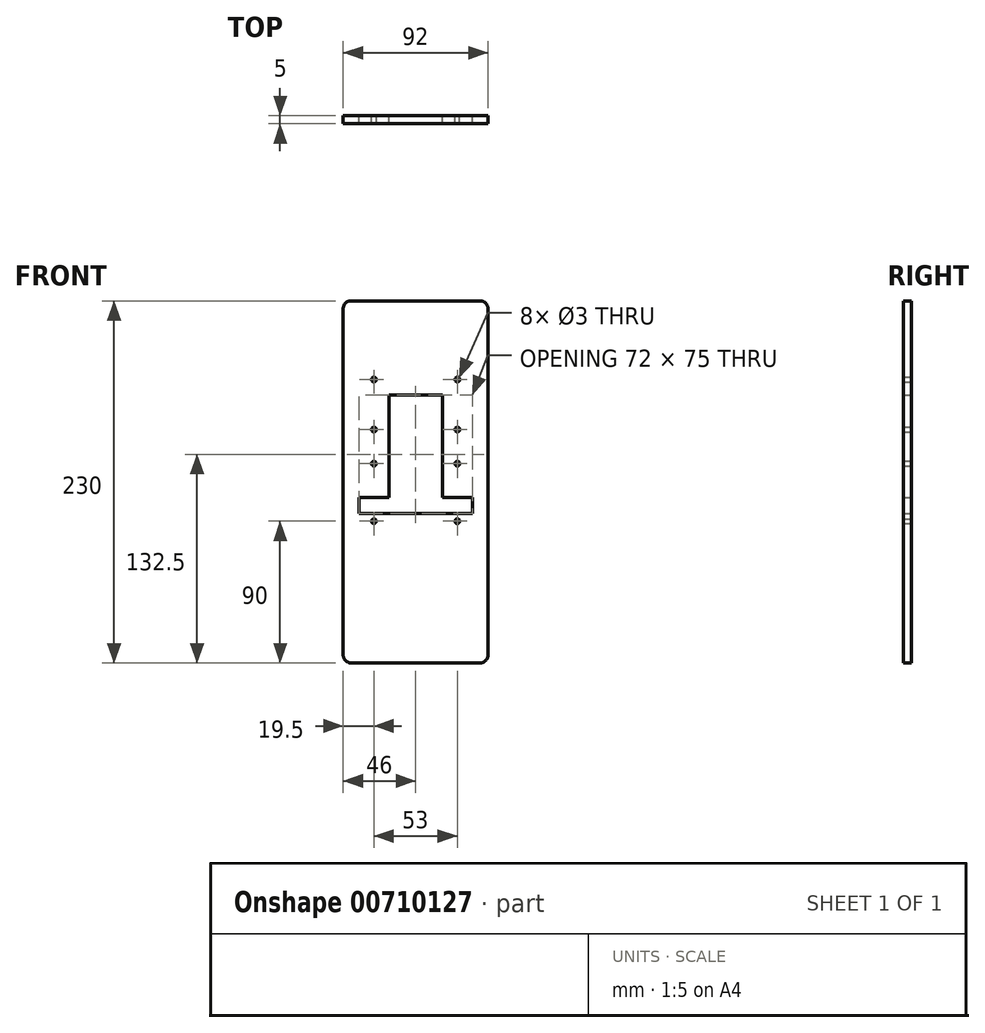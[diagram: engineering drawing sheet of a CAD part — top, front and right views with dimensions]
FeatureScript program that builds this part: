
annotation { "Feature Type Name" : "Feature", "Feature Type Description" : "" }
export const myFeature = defineFeature(function(context is Context, id is Id, definition is map)
    precondition{}
    {
        {
            var Q0;
            Q0=qCreatedBy(makeId("Front.planeOp"),FACE);
            var sketch = newSketch(context, id + "F0", { "sketchPlane" : qUnion([Q0])});
            skLineSegment(sketch, "E0.bottom", {"start": v(0, 0) * mm, "end": v(92, 0) * mm});
            skLineSegment(sketch, "E0.top", {"start": v(0, 230) * mm, "end": v(92, 230) * mm});
            skLineSegment(sketch, "E0.left", {"start": v(0, 0) * mm, "end": v(0, 230) * mm});
            skLineSegment(sketch, "E0.right", {"start": v(92, 0) * mm, "end": v(92, 230) * mm});
            skLineSegment(sketch, "E1", {"start": v(46, 0) * mm, "end": v(46, 95) * mm, "construction": true});
            skLineSegment(sketch, "E2", {"start": v(46, 95) * mm, "end": v(10, 95) * mm, "construction": true});
            skLineSegment(sketch, "E3.bottom", {"start": v(10, 95) * mm, "end": v(82, 95) * mm});
            skLineSegment(sketch, "E3.top", {"start": v(10, 105) * mm, "end": v(82, 105) * mm});
            skLineSegment(sketch, "E3.left", {"start": v(10, 95) * mm, "end": v(10, 105) * mm});
            skLineSegment(sketch, "E3.right", {"start": v(82, 95) * mm, "end": v(82, 105) * mm});
            skLineSegment(sketch, "E4", {"start": v(46, 105) * mm, "end": v(29, 105) * mm, "construction": true});
            skLineSegment(sketch, "E5.bottom", {"start": v(29, 105) * mm, "end": v(63, 105) * mm, "construction": true});
            skLineSegment(sketch, "E5.top", {"start": v(29, 170) * mm, "end": v(63, 170) * mm});
            skLineSegment(sketch, "E5.left", {"start": v(29, 105) * mm, "end": v(29, 170) * mm});
            skLineSegment(sketch, "E5.right", {"start": v(63, 105) * mm, "end": v(63, 170) * mm});
            skLineSegment(sketch, "E6", {"start": v(29, 105) * mm, "end": v(19.5, 105) * mm, "construction": true});
            skLineSegment(sketch, "E7", {"start": v(63, 105) * mm, "end": v(72.5, 105) * mm, "construction": true});
            skLineSegment(sketch, "E8", {"start": v(46, 105) * mm, "end": v(46, 90) * mm, "construction": true});
            skLineSegment(sketch, "E9", {"start": v(46, 90) * mm, "end": v(72.5, 90) * mm, "construction": true});
            skLineSegment(sketch, "E10", {"start": v(72.5, 90) * mm, "end": v(72.5, 180) * mm, "construction": true});
            skLineSegment(sketch, "E11", {"start": v(72.5, 105) * mm, "end": v(72.5, 126.6) * mm, "construction": true});
            skLineSegment(sketch, "E12", {"start": v(72.5, 148.2) * mm, "end": v(72.5, 126.6) * mm, "construction": true});
            skLineSegment(sketch, "E13", {"start": v(19.5, 105) * mm, "end": v(19.5, 126.6) * mm, "construction": true});
            skLineSegment(sketch, "E14", {"start": v(19.5, 126.6) * mm, "end": v(19.5, 148.2) * mm, "construction": true});
            skCircle(sketch, "E15", {"center": v(19.5, 90) * mm, "radius": 1.5 * mm});
            skCircle(sketch, "E16", {"center": v(72.5, 90) * mm, "radius": 1.5 * mm});
            skCircle(sketch, "E17", {"center": v(72.5, 126.6) * mm, "radius": 1.5 * mm});
            skCircle(sketch, "E18", {"center": v(72.5, 148.2) * mm, "radius": 1.5 * mm});
            skCircle(sketch, "E19", {"center": v(19.5, 148.2) * mm, "radius": 1.5 * mm});
            skCircle(sketch, "E20", {"center": v(19.5, 126.6) * mm, "radius": 1.5 * mm});
            skCircle(sketch, "E21", {"center": v(19.5, 180) * mm, "radius": 1.5 * mm});
            skCircle(sketch, "E22", {"center": v(72.5, 180) * mm, "radius": 1.5 * mm});
            skLineSegment(sketch, "E23", {"start": v(19.5, 180) * mm, "end": v(19.5, 90) * mm, "construction": true});
            skLineSegment(sketch, "E24", {"start": v(19.5, 90) * mm, "end": v(46, 90) * mm, "construction": true});
            skLineSegment(sketch, "E25", {"start": v(46, 90) * mm, "end": v(46, 105) * mm, "construction": true});
            skLineSegment(sketch, "E26", {"start": v(46, 90) * mm, "end": v(0, 90) * mm, "construction": true});
            skLineSegment(sketch, "E27", {"start": v(0, 90) * mm, "end": v(19.5, 90) * mm, "construction": true});
            skSolve(sketch);
        }
        {
            var Q0;
            Q0=makeQuery(id+"F0.imprint","IMPRINT",FACE,{"disambiguationData":[TD([[makeQuery(id+"F0.imprint","IMPRINT",EDGE,{"derivedFrom":sQuery(id+"F0.wireOp",EDGE,"E0.bottom")}),1.0]])]});
            extrude(context, id + "F1", {"entities" : qUnion([Q0]), "depth" : 5 * mm, "offsetDistance" : 25 * mm});
        }
        {
            var Q0;
            Q0=makeQuery(id+"F1.opExtrude","SWEPT_EDGE",EDGE,{"disambiguationData":[OSD([sQuery(id+"F0.wireOp",EDGE,"E0.top"),sQuery(id+"F0.wireOp",EDGE,"E0.right")])]});
            var Q1;
            Q1=makeQuery(id+"F1.opExtrude","SWEPT_EDGE",EDGE,{"disambiguationData":[OSD([sQuery(id+"F0.wireOp",EDGE,"E0.top"),sQuery(id+"F0.wireOp",EDGE,"E0.left")])]});
            var Q2;
            Q2=makeQuery(id+"F1.opExtrude","SWEPT_EDGE",EDGE,{"disambiguationData":[OSD([sQuery(id+"F0.wireOp",EDGE,"E0.bottom"),sQuery(id+"F0.wireOp",EDGE,"E0.left")])]});
            var Q3;
            Q3=makeQuery(id+"F1.opExtrude","SWEPT_EDGE",EDGE,{"disambiguationData":[OSD([sQuery(id+"F0.wireOp",EDGE,"E0.bottom"),sQuery(id+"F0.wireOp",EDGE,"E0.right")])]});
            fillet(context, id + "F2", {"entities" : qUnion([Q0, Q1, Q2, Q3]), "radius" : 5 * mm, "tangentPropagation" : true, "allowEdgeOverflow" : false});
        }
    });
